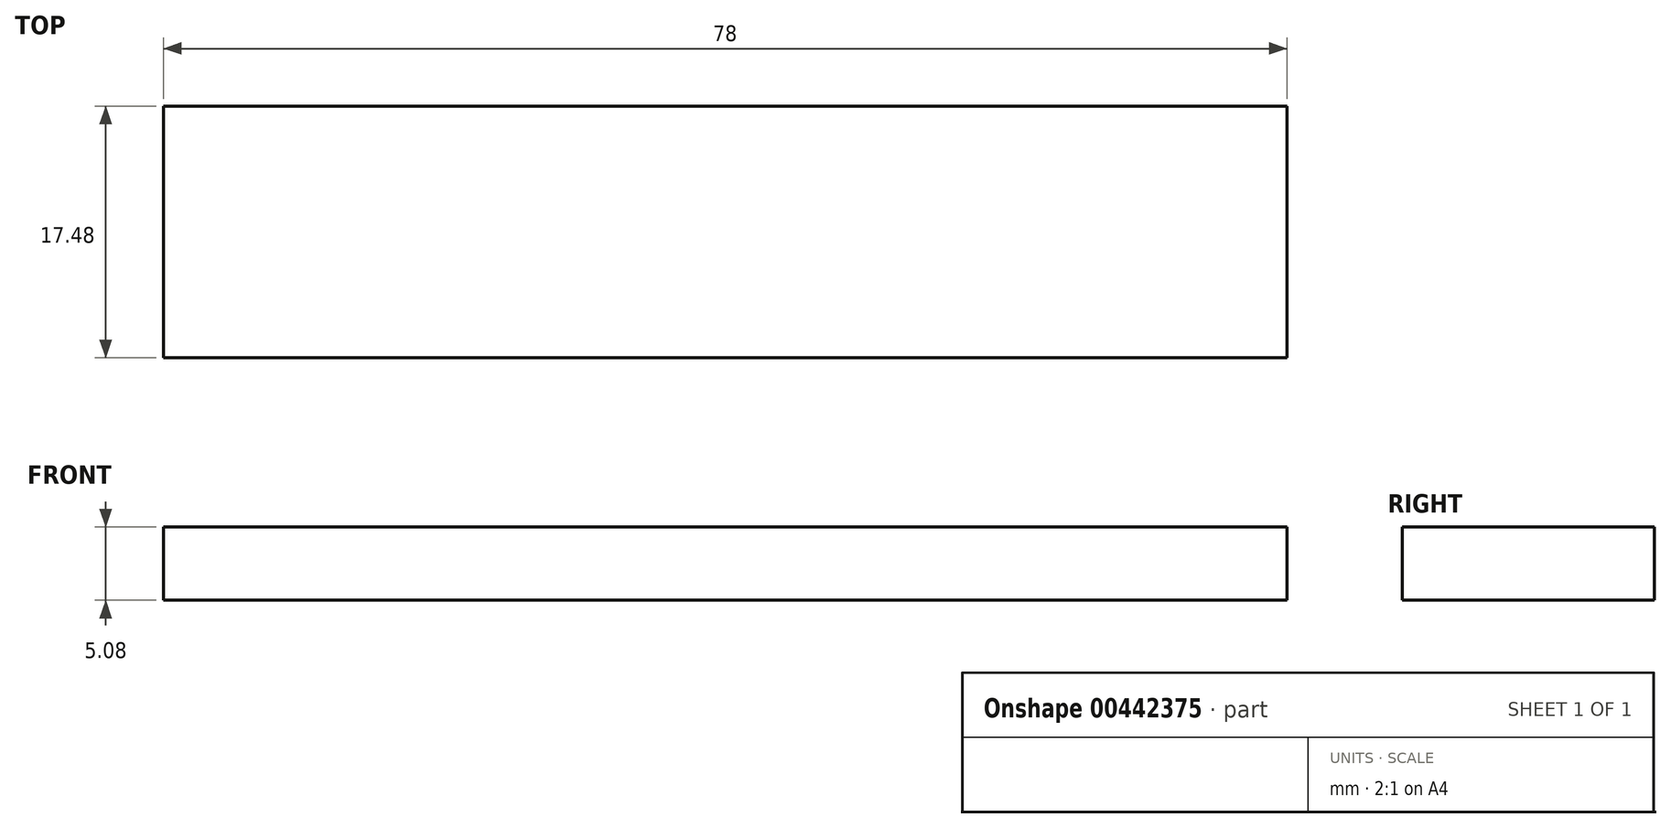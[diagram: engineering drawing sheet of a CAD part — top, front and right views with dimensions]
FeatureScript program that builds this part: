
annotation { "Feature Type Name" : "Feature", "Feature Type Description" : "" }
export const myFeature = defineFeature(function(context is Context, id is Id, definition is map)
    precondition{}
    {
        {
            var Q0;
            Q0=qCreatedBy(makeId("Top.planeOp"),FACE);
            var sketch = newSketch(context, id + "F0", { "sketchPlane" : qUnion([Q0])});
            skLineSegment(sketch, "E0.bottom", {"start": v(-39, 8.74) * mm, "end": v(39, 8.74) * mm});
            skLineSegment(sketch, "E0.top", {"start": v(-39, -8.74) * mm, "end": v(39, -8.74) * mm});
            skLineSegment(sketch, "E0.left", {"start": v(-39, 8.74) * mm, "end": v(-39, -8.74) * mm});
            skLineSegment(sketch, "E0.right", {"start": v(39, 8.74) * mm, "end": v(39, -8.74) * mm});
            skPoint(sketch, "E0.middle", {"position": v(0, 0) * mm});
            skSolve(sketch);
        }
        {
            var Q0;
            Q0 = qSketchRegion(id + "F0", true);
            extrude(context, id + "F1", {"entities" : qUnion([Q0]), "depth" : 5.08 * mm});
        }
    });
